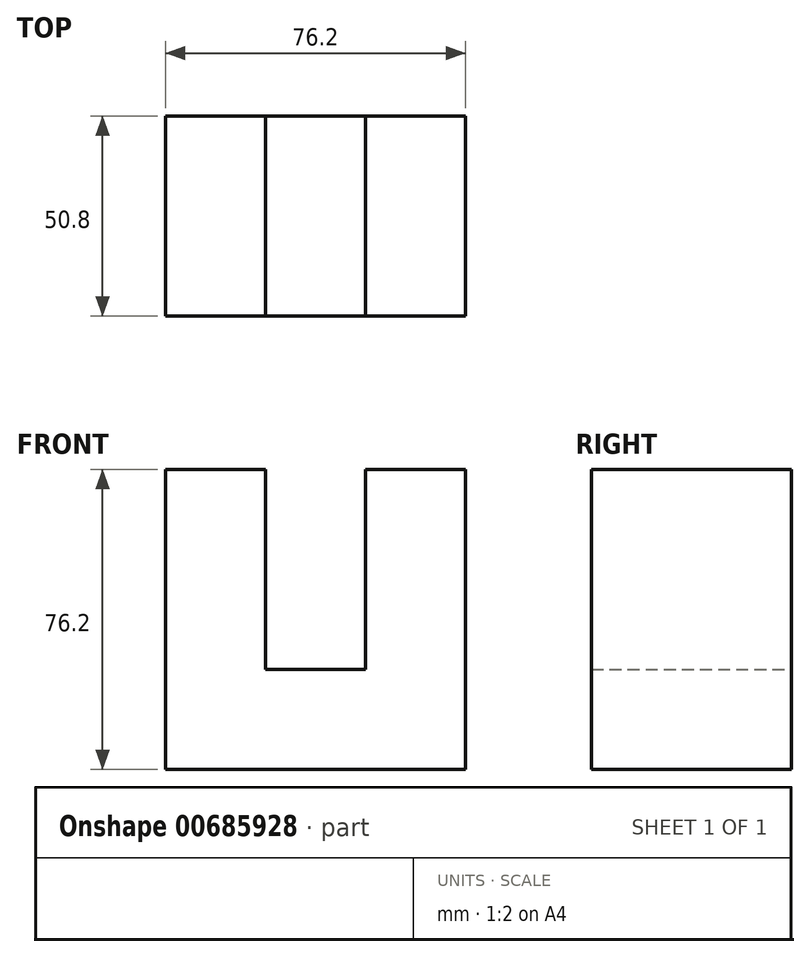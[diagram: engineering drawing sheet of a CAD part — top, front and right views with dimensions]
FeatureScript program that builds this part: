
annotation { "Feature Type Name" : "Feature", "Feature Type Description" : "" }
export const myFeature = defineFeature(function(context is Context, id is Id, definition is map)
    precondition{}
    {
        {
            var Q0;
            Q0=qCreatedBy(makeId("Front.planeOp"),FACE);
            var sketch = newSketch(context, id + "F0", { "sketchPlane" : qUnion([Q0])});
            skLineSegment(sketch, "E0", {"start": v(0, 0) * mm, "end": v(0, -76.2) * mm});
            skLineSegment(sketch, "E1", {"start": v(0, -76.2) * mm, "end": v(76.2, -76.2) * mm});
            skLineSegment(sketch, "E2", {"start": v(76.2, -76.2) * mm, "end": v(76.2, 0) * mm});
            skLineSegment(sketch, "E3", {"start": v(0, 0) * mm, "end": v(25.4, 0) * mm});
            skLineSegment(sketch, "E4", {"start": v(76.2, 0) * mm, "end": v(50.8, 0) * mm});
            skLineSegment(sketch, "E5", {"start": v(25.4, 0) * mm, "end": v(25.4, -50.8) * mm});
            skLineSegment(sketch, "E6", {"start": v(50.8, 0) * mm, "end": v(50.8, -50.8) * mm});
            skLineSegment(sketch, "E7", {"start": v(25.4, -50.8) * mm, "end": v(52.98, -50.8) * mm});
            skSolve(sketch);
        }
        {
            var Q0;
            Q0 = qSketchRegion(id + "F0", true);
            extrude(context, id + "F1", {"entities" : qUnion([Q0]), "depth" : 50.8 * mm, "offsetDistance" : 25.4 * mm});
        }
    });
